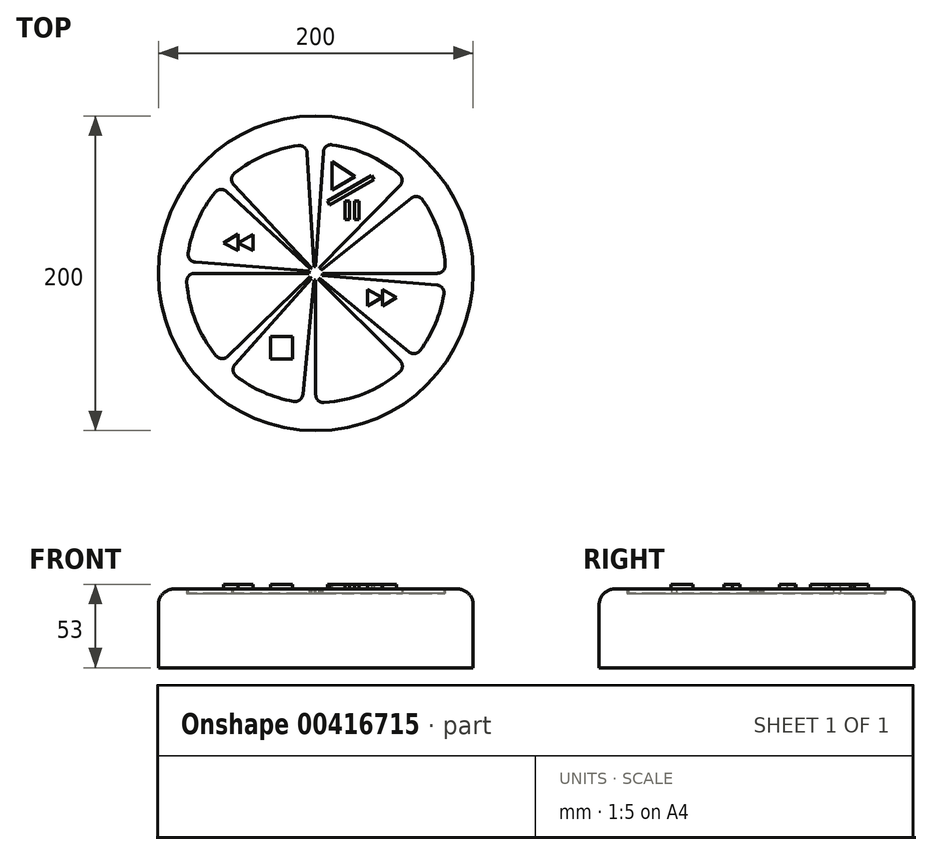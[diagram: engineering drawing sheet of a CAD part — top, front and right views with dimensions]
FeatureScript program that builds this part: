
annotation { "Feature Type Name" : "Feature", "Feature Type Description" : "" }
export const myFeature = defineFeature(function(context is Context, id is Id, definition is map)
    precondition{}
    {
        {
            var Q0;
            Q0=qCreatedBy(makeId("Top.planeOp"),FACE);
            var sketch = newSketch(context, id + "F0", { "sketchPlane" : qUnion([Q0])});
            skCircle(sketch, "E0", {"center": v(0, 0) * mm, "radius": 100 * mm});
            skSolve(sketch);
        }
        {
            var Q0;
            Q0 = qSketchRegion(id + "F0", true);
            extrude(context, id + "F1", {"entities" : qUnion([Q0]), "depth" : 50 * mm});
        }
        {
            var Q0;
            Q0=makeQuery(id+"F1.opExtrude","CAP_EDGE",EDGE,{"disambiguationData":[OSD([sQuery(id+"F0.wireOp",EDGE,"E0")])],"isStart":false});
            fillet(context, id + "F2", {"entities" : qUnion([Q0]), "radius" : 10 * mm, "tangentPropagation" : true, "allowEdgeOverflow" : false});
        }
        {
            var Q0;
            Q0=makeQuery(id+"F1.opExtrude","CAP_FACE",FACE,{"disambiguationData":[OSD([sQuery(id+"F0.wireOp",EDGE,"E0")])],"isStart":false});
            extrude(context, id + "F3", {"entities" : qUnion([Q0]), "operationType" : NewBodyOperationType.REMOVE, "oppositeDirection" : true, "depth" : 3 * mm});
        }
        {
            var Q0;
            Q0=makeQuery(id+"F3.boolean.opBoolean","COPY",FACE,{"derivedFrom":makeQuery(id+"F3.opExtrude","CAP_FACE",FACE,{"disambiguationData":[OSD([sQuery(id+"F0.wireOp",EDGE,"E0")])],"isStart":false})});
            var sketch = newSketch(context, id + "F4", { "sketchPlane" : qUnion([Q0])});
            skArc(sketch, "E1", {"start": v(10.42, 81.6) * mm, "mid": v(33.07, 75.33) * mm, "end": v(53.02, 62.9) * mm});
            skArc(sketch, "E2", {"start": v(67.91, 46.6) * mm, "mid": v(77.84, 26.92) * mm, "end": v(82.2, 5.32) * mm});
            skArc(sketch, "E3", {"start": v(81.41, -13.24) * mm, "mid": v(76.01, -32.02) * mm, "end": v(66.35, -49) * mm});
            skArc(sketch, "E4", {"start": v(53.22, -62.85) * mm, "mid": v(30.83, -76.37) * mm, "end": v(5.32, -82.18) * mm});
            skArc(sketch, "E5", {"start": v(-14, -81.37) * mm, "mid": v(-33.3, -75.55) * mm, "end": v(-50.6, -65.23) * mm});
            skArc(sketch, "E6", {"start": v(-63.2, -52.4) * mm, "mid": v(-76.28, -30.34) * mm, "end": v(-81.92, -5.32) * mm});
            skArc(sketch, "E7", {"start": v(-81.04, 12.87) * mm, "mid": v(-75.02, 33.23) * mm, "end": v(-63.99, 51.37) * mm});
            skArc(sketch, "E8", {"start": v(-51.6, 63.52) * mm, "mid": v(-32.56, 75.08) * mm, "end": v(-11.1, 81.08) * mm});
            skCircle(sketch, "E9", {"center": v(0, 0) * mm, "radius": 4.27 * mm});
            skLineSegment(sketch, "E10", {"start": v(4.8, 76.97) * mm, "end": v(0, 4.27) * mm});
            skLineSegment(sketch, "E11", {"start": v(53.37, 55.58) * mm, "end": v(2.34, 3.58) * mm});
            skLineSegment(sketch, "E12", {"start": v(60.67, 47.68) * mm, "end": v(3.66, 2.2) * mm});
            skLineSegment(sketch, "E13", {"start": v(77.2, 0) * mm, "end": v(4.27, 0) * mm});
            skLineSegment(sketch, "E14", {"start": v(76.9, -7.46) * mm, "end": v(4.05, -1.37) * mm});
            skLineSegment(sketch, "E15", {"start": v(59.14, -49.89) * mm, "end": v(2.73, -3.29) * mm});
            skLineSegment(sketch, "E16", {"start": v(53.52, -55.5) * mm, "end": v(1.88, -3.84) * mm});
            skLineSegment(sketch, "E17", {"start": v(0, -77.2) * mm, "end": v(0, -4.27) * mm});
            skLineSegment(sketch, "E18", {"start": v(-8.18, -76.92) * mm, "end": v(-1.13, -4.12) * mm});
            skLineSegment(sketch, "E19", {"start": v(-51.28, -57.96) * mm, "end": v(-2.7, -3.3) * mm});
            skLineSegment(sketch, "E20", {"start": v(-55.85, -52.8) * mm, "end": v(-3.75, -2.05) * mm});
            skLineSegment(sketch, "E21", {"start": v(-76.93, 0) * mm, "end": v(-4.27, 0) * mm});
            skLineSegment(sketch, "E22", {"start": v(-76.48, 7.1) * mm, "end": v(-4, 1.52) * mm});
            skLineSegment(sketch, "E23", {"start": v(-56.7, 51.91) * mm, "end": v(-3.32, 2.7) * mm});
            skLineSegment(sketch, "E24", {"start": v(-52.1, 56.21) * mm, "end": v(-2.54, 3.44) * mm});
            skLineSegment(sketch, "E25", {"start": v(-5.43, 76.42) * mm, "end": v(-1.23, 4.1) * mm});
            skPoint(sketch, "E26.visualSharp", {"position": v(-55.66, 60) * mm});
            skArc(sketch, "E26.filletArc", {"start": v(-51.6, 63.52) * mm, "mid": v(-53.44, 59.97) * mm, "end": v(-52.1, 56.21) * mm});
            skPoint(sketch, "E27.visualSharp", {"position": v(-5.74, 81.64) * mm});
            skArc(sketch, "E27.filletArc", {"start": v(-5.43, 76.42) * mm, "mid": v(-7.25, 80) * mm, "end": v(-11.1, 81.08) * mm});
            skPoint(sketch, "E28.visualSharp", {"position": v(5.13, 82.1) * mm});
            skArc(sketch, "E28.filletArc", {"start": v(10.42, 81.6) * mm, "mid": v(6.6, 80.5) * mm, "end": v(4.8, 76.97) * mm});
            skPoint(sketch, "E29.visualSharp", {"position": v(57.02, 59.3) * mm});
            skArc(sketch, "E29.filletArc", {"start": v(53.37, 55.58) * mm, "mid": v(54.8, 59.31) * mm, "end": v(53.02, 62.9) * mm});
            skPoint(sketch, "E30.visualSharp", {"position": v(64.74, 50.92) * mm});
            skArc(sketch, "E30.filletArc", {"start": v(67.91, 46.6) * mm, "mid": v(64.53, 48.72) * mm, "end": v(60.67, 47.68) * mm});
            skPoint(sketch, "E31.visualSharp", {"position": v(82.36, 0) * mm});
            skArc(sketch, "E31.filletArc", {"start": v(77.2, 0) * mm, "mid": v(80.85, 1.58) * mm, "end": v(82.2, 5.32) * mm});
            skPoint(sketch, "E32.visualSharp", {"position": v(82.1, -7.9) * mm});
            skArc(sketch, "E32.filletArc", {"start": v(81.41, -13.24) * mm, "mid": v(80.42, -9.36) * mm, "end": v(76.9, -7.46) * mm});
            skPoint(sketch, "E33.visualSharp", {"position": v(63.08, -53.14) * mm});
            skArc(sketch, "E33.filletArc", {"start": v(59.14, -49.89) * mm, "mid": v(62.94, -51) * mm, "end": v(66.35, -49) * mm});
            skPoint(sketch, "E34.visualSharp", {"position": v(57.24, -59.21) * mm});
            skArc(sketch, "E34.filletArc", {"start": v(53.22, -62.85) * mm, "mid": v(54.98, -59.24) * mm, "end": v(53.52, -55.5) * mm});
            skPoint(sketch, "E35.visualSharp", {"position": v(0, -82.35) * mm});
            skArc(sketch, "E35.filletArc", {"start": v(0, -77.2) * mm, "mid": v(1.58, -80.84) * mm, "end": v(5.32, -82.18) * mm});
            skPoint(sketch, "E36.visualSharp", {"position": v(-8.68, -82.1) * mm});
            skArc(sketch, "E36.filletArc", {"start": v(-14, -81.37) * mm, "mid": v(-10.13, -80.41) * mm, "end": v(-8.18, -76.92) * mm});
            skPoint(sketch, "E37.visualSharp", {"position": v(-54.72, -61.83) * mm});
            skArc(sketch, "E37.filletArc", {"start": v(-51.28, -57.96) * mm, "mid": v(-52.52, -61.74) * mm, "end": v(-50.6, -65.23) * mm});
            skPoint(sketch, "E38.visualSharp", {"position": v(-59.6, -56.45) * mm});
            skArc(sketch, "E38.filletArc", {"start": v(-63.2, -52.4) * mm, "mid": v(-59.6, -54.2) * mm, "end": v(-55.85, -52.8) * mm});
            skPoint(sketch, "E39.visualSharp", {"position": v(-82.1, 0) * mm});
            skArc(sketch, "E39.filletArc", {"start": v(-76.93, 0) * mm, "mid": v(-80.58, -1.58) * mm, "end": v(-81.92, -5.32) * mm});
            skPoint(sketch, "E40.visualSharp", {"position": v(-81.71, 7.5) * mm});
            skArc(sketch, "E40.filletArc", {"start": v(-81.04, 12.87) * mm, "mid": v(-80.03, 8.99) * mm, "end": v(-76.48, 7.1) * mm});
            skPoint(sketch, "E41.visualSharp", {"position": v(-60.5, 55.42) * mm});
            skArc(sketch, "E41.filletArc", {"start": v(-56.7, 51.91) * mm, "mid": v(-60.46, 53.22) * mm, "end": v(-63.99, 51.37) * mm});
            skSolve(sketch);
        }
        {
            var Q0;
            Q0=makeQuery(id+"F4.imprint","IMPRINT",FACE,{"disambiguationData":[TD([[makeQuery(id+"F4.imprint","IMPRINT",EDGE,{"derivedFrom":sQuery(id+"F4.wireOp",EDGE,"E1")}),-1.0]])]});
            var Q1;
            Q1=makeQuery(id+"F4.imprint","IMPRINT",FACE,{"disambiguationData":[TD([[makeQuery(id+"F4.imprint","IMPRINT",EDGE,{"derivedFrom":sQuery(id+"F4.wireOp",EDGE,"E2")}),-1.0]])]});
            var Q2;
            Q2=makeQuery(id+"F4.imprint","IMPRINT",FACE,{"disambiguationData":[TD([[makeQuery(id+"F4.imprint","IMPRINT",EDGE,{"derivedFrom":sQuery(id+"F4.wireOp",EDGE,"E3")}),-1.0]])]});
            var Q3;
            Q3=makeQuery(id+"F4.imprint","IMPRINT",FACE,{"disambiguationData":[TD([[makeQuery(id+"F4.imprint","IMPRINT",EDGE,{"derivedFrom":sQuery(id+"F4.wireOp",EDGE,"E4")}),-1.0]])]});
            var Q4;
            Q4=makeQuery(id+"F4.imprint","IMPRINT",FACE,{"disambiguationData":[TD([[makeQuery(id+"F4.imprint","IMPRINT",EDGE,{"derivedFrom":sQuery(id+"F4.wireOp",EDGE,"E5")}),-1.0]])]});
            var Q5;
            Q5=makeQuery(id+"F4.imprint","IMPRINT",FACE,{"disambiguationData":[TD([[makeQuery(id+"F4.imprint","IMPRINT",EDGE,{"derivedFrom":sQuery(id+"F4.wireOp",EDGE,"E6")}),-1.0]])]});
            var Q6;
            Q6=makeQuery(id+"F4.imprint","IMPRINT",FACE,{"disambiguationData":[TD([[makeQuery(id+"F4.imprint","IMPRINT",EDGE,{"derivedFrom":sQuery(id+"F4.wireOp",EDGE,"E7")}),-1.0]])]});
            var Q7;
            Q7=makeQuery(id+"F4.imprint","IMPRINT",FACE,{"disambiguationData":[TD([[makeQuery(id+"F4.imprint","IMPRINT",EDGE,{"derivedFrom":sQuery(id+"F4.wireOp",EDGE,"E8")}),-1.0]])]});
            extrude(context, id + "F5", {"entities" : qUnion([Q0, Q1, Q2, Q3, Q4, Q5, Q6, Q7]), "operationType" : NewBodyOperationType.ADD, "depth" : 3 * mm});
        }
        {
            var Q0;
            Q0=makeQuery(id+"F5.opExtrude","CAP_FACE",FACE,{"disambiguationData":[OSD([sQuery(id+"F4.wireOp",EDGE,"E1"),sQuery(id+"F4.wireOp",EDGE,"E9"),sQuery(id+"F4.wireOp",EDGE,"E10"),sQuery(id+"F4.wireOp",EDGE,"E11"),sQuery(id+"F4.wireOp",EDGE,"E28.filletArc"),sQuery(id+"F4.wireOp",EDGE,"E29.filletArc")])],"isStart":false});
            var sketch = newSketch(context, id + "F6", { "sketchPlane" : qUnion([Q0])});
            skSolve(sketch);
        }
        {
            var Q0;
            Q0=makeQuery(id+"F6.imprint","IMPRINT",FACE,{"disambiguationData":[TD([[makeQuery(id+"F6.imprint","IMPRINT",EDGE,{"derivedFrom":makeQuery(id+"F5.opExtrude","CAP_EDGE",EDGE,{"disambiguationData":[OSD([sQuery(id+"F4.wireOp",EDGE,"E1")])],"isStart":false})}),-1.0]])]});
            var sketch = newSketch(context, id + "F7", { "sketchPlane" : qUnion([Q0])});
            skLineSegment(sketch, "E42", {"start": v(10.37, 71) * mm, "end": v(10.37, 52.86) * mm});
            skLineSegment(sketch, "E43", {"start": v(10.37, 52.86) * mm, "end": v(24.8, 61.31) * mm});
            skLineSegment(sketch, "E44", {"start": v(24.8, 61.31) * mm, "end": v(10.37, 71) * mm});
            skLineSegment(sketch, "E45", {"start": v(7.48, 45.84) * mm, "end": v(35.53, 62.14) * mm});
            skLineSegment(sketch, "E46", {"start": v(35.53, 62.14) * mm, "end": v(36.95, 59.68) * mm});
            skLineSegment(sketch, "E47", {"start": v(36.95, 59.68) * mm, "end": v(8.8, 43.33) * mm});
            skLineSegment(sketch, "E48", {"start": v(8.8, 43.33) * mm, "end": v(7.48, 45.84) * mm});
            skLineSegment(sketch, "E49", {"start": v(18.62, 45.84) * mm, "end": v(18.62, 34.09) * mm});
            skLineSegment(sketch, "E50", {"start": v(18.62, 34.09) * mm, "end": v(21.3, 34.09) * mm});
            skLineSegment(sketch, "E51", {"start": v(21.3, 34.09) * mm, "end": v(21.3, 45.84) * mm});
            skLineSegment(sketch, "E52", {"start": v(21.3, 45.84) * mm, "end": v(18.62, 45.84) * mm});
            skLineSegment(sketch, "E53", {"start": v(24.68, 45.84) * mm, "end": v(24.68, 34.09) * mm});
            skLineSegment(sketch, "E54", {"start": v(24.68, 34.09) * mm, "end": v(27.36, 34.09) * mm});
            skLineSegment(sketch, "E55", {"start": v(27.36, 34.09) * mm, "end": v(27.36, 45.84) * mm});
            skLineSegment(sketch, "E56", {"start": v(27.36, 45.84) * mm, "end": v(24.68, 45.84) * mm});
            skLineSegment(sketch, "E57.bottom", {"start": v(-14.68, -40.3) * mm, "end": v(-28.68, -40.3) * mm});
            skLineSegment(sketch, "E57.top", {"start": v(-14.68, -54.3) * mm, "end": v(-28.68, -54.3) * mm});
            skLineSegment(sketch, "E57.left", {"start": v(-14.68, -40.3) * mm, "end": v(-14.68, -54.3) * mm});
            skLineSegment(sketch, "E57.right", {"start": v(-28.68, -40.3) * mm, "end": v(-28.68, -54.3) * mm});
            skPoint(sketch, "E57.middle", {"position": v(-21.68, -47.3) * mm});
            skLineSegment(sketch, "E58", {"start": v(32.8, -10.44) * mm, "end": v(32.8, -20.7) * mm});
            skLineSegment(sketch, "E59", {"start": v(32.8, -20.7) * mm, "end": v(42.08, -15.27) * mm});
            skLineSegment(sketch, "E60", {"start": v(42.08, -15.27) * mm, "end": v(32.8, -10.44) * mm});
            skLineSegment(sketch, "E61", {"start": v(42.28, -10.44) * mm, "end": v(42.28, -20.9) * mm});
            skLineSegment(sketch, "E62", {"start": v(42.28, -20.9) * mm, "end": v(51.36, -15.27) * mm});
            skLineSegment(sketch, "E63", {"start": v(51.36, -15.27) * mm, "end": v(42.28, -10.44) * mm});
            skLineSegment(sketch, "E64", {"start": v(-39.96, 14.39) * mm, "end": v(-39.96, 24.65) * mm});
            skLineSegment(sketch, "E65", {"start": v(-39.96, 24.65) * mm, "end": v(-49.24, 19.22) * mm});
            skLineSegment(sketch, "E66", {"start": v(-49.24, 19.22) * mm, "end": v(-39.96, 14.39) * mm});
            skLineSegment(sketch, "E67", {"start": v(-49.44, 14.39) * mm, "end": v(-49.44, 24.85) * mm});
            skLineSegment(sketch, "E68", {"start": v(-49.44, 24.85) * mm, "end": v(-58.51, 19.22) * mm});
            skLineSegment(sketch, "E69", {"start": v(-58.51, 19.22) * mm, "end": v(-49.44, 14.39) * mm});
            skSolve(sketch);
        }
        {
            var Q0;
            Q0 = qSketchRegion(id + "F7", true);
            extrude(context, id + "F8", {"entities" : qUnion([Q0]), "operationType" : NewBodyOperationType.ADD, "depth" : 3 * mm});
        }
    });
